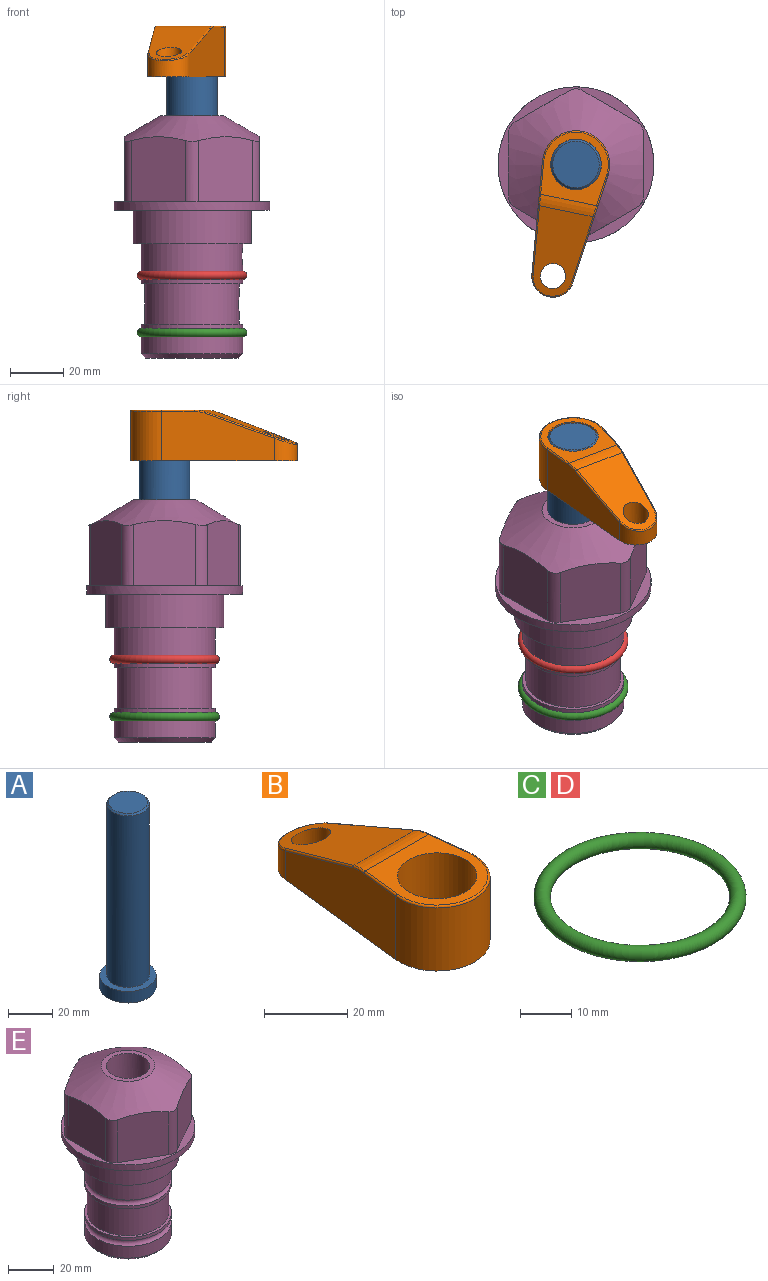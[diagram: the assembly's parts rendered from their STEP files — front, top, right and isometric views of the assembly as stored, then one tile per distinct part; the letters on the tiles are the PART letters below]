
ASSEMBLY  parts=5 mates=3
PART A: 6 faces, bbox 25.4x25.4x101.6 mm
  f0: plane 17.46x17.46mm, normal (0,0,1), area 239.5mm2, adj f5
  f1: plane 25.4x25.4mm, normal (0,0,-1), area 506.7mm2, adj f2
  f2: cylinder r=12.7mm len=25.4mm, axis (0,0,1), area 506.7mm2, adj f1,f3
  f3: plane 25.4x25.4mm, normal (0,0,1), area 221.7mm2, adj f2,f4
  f4: cylinder r=9.53mm len=94.46mm, axis (0,0,1), area 5653mm2, adj f3,f5
  f5: cone r=8.73mm half-angle=45deg, axis (0,0,-1), area 64.4mm2, adj f0,f4
PART B: 44 faces, bbox 27.5x64.5x19.1 mm
  f0: plane 2.3x0.95mm, normal (0,0,-1), area 1mm2, adj f25,f30,f34
  f1: plane 63.5x25.4mm, normal (0,0,-1), area 561.7mm2, adj f2,f3,f4,f5,f6,f7,f19,f20
  f2: cylinder r=12.7mm len=25.4mm, axis (0,0,-1), area 792.2mm2, adj f1,f3,f5,f13
  f3: plane 42.33x18.54mm, normal (0.99,0.11,0), area 647mm2, adj f1,f2,f4,f11,f12,f14
  f4: cylinder r=7.94mm len=15.78mm, axis (0,0,-1), area 158.6mm2, adj f1,f3,f5,f16
  f5: plane 42.33x18.54mm, normal (-0.99,0.11,0), area 647mm2, adj f1,f2,f4,f15,f17,f18
  f6: cylinder r=9.53mm len=19.05mm, axis (0,0,-1), area 1140.1mm2, adj f1,f8
  f7: cylinder r=4.76mm len=10.98mm, axis (0,0,-1), area 276.1mm2, adj f1,f9
  f8: plane 25.83x24.38mm, normal (0,0,1), area 262.2mm2, adj f6,f10,f11,f13,f15
  f9: plane 32.49x20.55mm, normal (0,0.34,0.94), area 489.9mm2, adj f7,f10,f14,f16,f18
  f10: cylinder r=12.7mm len=21.49mm, axis (-1,0,0), area 93.2mm2, adj f8,f9,f12,f17
  f11: cylinder r=0.51mm len=12.34mm, axis (0.11,-0.99,0), area 9.9mm2, adj f3,f8,f12,f13
  f12: bspline ~7.62x1.64mm, area 3.5mm2, adj f3,f10,f11,f14
  f13: torus R=12.19mm, axis (0,0,1), area 33.6mm2, adj f2,f8,f11,f15
  f14: cylinder r=0.51mm len=26.01mm, axis (0.1,-0.93,0.34), area 21.6mm2, adj f3,f9,f12,f16
  f15: cylinder r=0.51mm len=12.34mm, axis (0.11,0.99,0), area 9.9mm2, adj f5,f8,f13,f17
  f16: bspline ~15.78x7.05mm, area 15.7mm2, adj f4,f9,f14,f18
  f17: bspline ~7.62x1.64mm, area 3.5mm2, adj f5,f10,f15,f18
  f18: cylinder r=0.51mm len=26.01mm, axis (0.1,0.93,-0.34), area 21.6mm2, adj f5,f9,f16,f17
  f19: plane 21.6x14.29mm, normal (-0.99,-0.11,0), area 242.6mm2, adj f1,f26,f28,f34,f36,f38
  f20: plane 21.6x14.29mm, normal (0.99,-0.11,0), area 242.6mm2, adj f1,f27,f29,f37,f39,f41
  f21: cylinder r=12.7mm len=14.29mm, axis (0,0,-1), area 173.2mm2, adj f1,f26,f27,f30,f31,f33
  f22: cylinder r=7.94mm len=7.63mm, axis (0,0,-1), area 53.8mm2, adj f1,f28,f29,f42
  f23: plane 2.3x0.95mm, normal (0,0,-1), area 1mm2, adj f25,f33,f37
  f24: plane 17.94x12.32mm, normal (0,-0.34,-0.94), area 191.2mm2, adj f25,f38,f41,f42
  f25: cylinder r=9.53mm len=12.93mm, axis (-1,0,0), area 37.5mm2, adj f0,f23,f24,f31,f36,f39
  f26: cylinder r=1.59mm len=14.29mm, axis (0,0,-1), area 49mm2, adj f1,f19,f21,f32
  f27: cylinder r=1.59mm len=14.29mm, axis (0,0,-1), area 49mm2, adj f1,f20,f21,f35
  f28: cylinder r=1.59mm len=7.28mm, axis (0,0,-1), area 22.1mm2, adj f1,f19,f22,f40
  f29: cylinder r=1.59mm len=7.28mm, axis (0,0,-1), area 22.1mm2, adj f1,f20,f22,f43
  f30: torus R=14.29mm, axis (0,0,1), area 5.8mm2, adj f0,f21,f31,f32
  f31: bspline ~11.06x2.73mm, area 20.8mm2, adj f21,f25,f30,f33
  f32: sphere r=1.59mm, area 5.4mm2, adj f26,f30,f34
  f33: torus R=14.29mm, axis (0,0,1), area 5.8mm2, adj f21,f23,f31,f35
  f34: cylinder r=1.59mm len=1.68mm, axis (-0.11,0.99,0), area 2.4mm2, adj f0,f19,f32,f36
  f35: sphere r=1.59mm, area 5.4mm2, adj f27,f33,f37
  f36: bspline ~5.82x2.33mm, area 7.7mm2, adj f19,f25,f34,f38
  f37: cylinder r=1.59mm len=1.68mm, axis (0.11,0.99,0), area 2.4mm2, adj f20,f23,f35,f39
  f38: cylinder r=1.59mm len=18.33mm, axis (0.1,-0.93,0.34), area 46.7mm2, adj f19,f24,f36,f40
  f39: bspline ~5.82x2.33mm, area 7.7mm2, adj f20,f25,f37,f41
  f40: sphere r=1.59mm, area 3.6mm2, adj f28,f38,f42
  f41: cylinder r=1.59mm len=18.33mm, axis (0.1,0.93,-0.34), area 46.7mm2, adj f20,f24,f39,f43
  f42: bspline ~8.31x1.84mm, area 15.3mm2, adj f22,f24,f40,f43
  f43: sphere r=1.59mm, area 3.6mm2, adj f29,f41,f42
PART C: 1 faces, bbox 44.7x44.7x3.2 mm
  f0: torus R=19.05mm, axis (0,0,1), area 1193.9mm2
PART D: same geometry as C
PART E: 36 faces, bbox 58.7x58.7x91.2 mm
  f0: cylinder r=17.78mm len=35.56mm, axis (0,0,1), area 1670.8mm2, adj f23,f24,f31
  f1: cylinder r=19.05mm len=38.1mm, axis (0,0,1), area 1191.9mm2, adj f26,f27,f30
  f2: plane 58.66x58.66mm, normal (0,0,-1), area 1150.6mm2, adj f3,f28
  f3: cylinder r=29.33mm len=58.66mm, axis (0,0,-1), area 585.1mm2, adj f2,f4
  f4: plane 58.66x58.66mm, normal (0,0,1), area 475.9mm2, adj f3,f5,f6,f7,f8,f9,f10,f11
  f5: plane 24.5x20.32mm, normal (-0.5,0.87,0), area 562.8mm2, adj f4,f15,f16,f17
  f6: plane 24.5x20.32mm, normal (0.5,0.87,0), area 562.8mm2, adj f4,f14,f15,f17
  f7: plane 24.5x23.48mm, normal (1,0,0), area 562.8mm2, adj f4,f13,f14,f17
  f8: plane 24.5x20.32mm, normal (0.5,-0.87,0), area 562.8mm2, adj f4,f12,f13,f17
  f9: plane 24.5x20.32mm, normal (-0.5,-0.87,0), area 562.8mm2, adj f4,f11,f12,f17
  f10: plane 24.5x23.48mm, normal (-1,0,0), area 562.8mm2, adj f4,f11,f16,f17
  f11: cylinder r=5.08mm len=23.01mm, axis (0,0,-1), area 121.2mm2, adj f4,f9,f10,f17
  f12: cylinder r=5.08mm len=23.01mm, axis (0,0,-1), area 121.2mm2, adj f4,f8,f9,f17
  f13: cylinder r=5.08mm len=23.01mm, axis (0,0,-1), area 121.2mm2, adj f4,f7,f8,f17
  f14: cylinder r=5.08mm len=23.01mm, axis (0,0,-1), area 121.2mm2, adj f4,f6,f7,f17
  f15: cylinder r=5.08mm len=23.01mm, axis (0,0,-1), area 121.2mm2, adj f4,f5,f6,f17
  f16: cylinder r=5.08mm len=23.01mm, axis (0,0,-1), area 121.2mm2, adj f4,f5,f10,f17
  f17: cone r=11.73mm half-angle=60deg, axis (0,0,-1), area 2071.8mm2, adj f5,f6,f7,f8,f9,f10,f11,f12
  f18: plane 23.46x23.46mm, normal (0,0,1), area 147.4mm2, adj f17,f35
  f19: plane 34.93x34.93mm, normal (0,0,-1), area 958mm2, adj f29
  f20: cylinder r=19.05mm len=38.1mm, axis (0,0,1), area 760.1mm2, adj f21,f29
  f21: torus R=19.05mm, axis (0,0,1), area 565.3mm2, adj f20,f22
  f22: cylinder r=19.05mm len=38.1mm, axis (0,0,1), area 190mm2, adj f21,f23
  f23: plane 38.1x38.1mm, normal (0,0,1), area 146.9mm2, adj f0,f22
  f24: plane 38.1x38.1mm, normal (0,0,-1), area 146.9mm2, adj f0,f25
  f25: cylinder r=19.05mm len=38.1mm, axis (0,0,1), area 190mm2, adj f24,f26
  f26: torus R=19.05mm, axis (0,0,1), area 565.3mm2, adj f1,f25
  f27: plane 44.45x44.45mm, normal (0,0,-1), area 411.7mm2, adj f1,f28
  f28: cylinder r=22.23mm len=44.45mm, axis (0,0,1), area 1773.5mm2, adj f2,f27
  f29: cone r=19.05mm half-angle=45deg, axis (0,0,1), area 257.5mm2, adj f19,f20
  f30: cylinder r=3.17mm len=6.75mm, axis (-1,0,0), area 128mm2, adj f1,f33
  f31: cylinder r=3.17mm len=6.35mm, axis (-1,0,0), area 102.5mm2, adj f0,f33
  f32: plane 25.4x25.4mm, normal (0,0,1), area 506.7mm2, adj f33
  f33: cylinder r=12.7mm len=66.42mm, axis (0,0,-1), area 5236.2mm2, adj f30,f31,f32,f34
  f34: cone r=9.53mm half-angle=30deg, axis (0,0,-1), area 443.4mm2, adj f33,f35
  f35: cylinder r=9.53mm len=19.05mm, axis (0,0,-1), area 849mm2, adj f18,f34
PLACE A rot(axis=(0,0,-1),101.7deg) t=(0,0,-4.35)mm
PLACE B rot(axis=(0,0,1),168.3deg) t=(0,0,50.26)mm
PLACE C t=(0,0,-21.59)mm
PLACE D at identity
PLACE E at identity fixed
MATE fastened C.f0 <-> E.f0  axis (0,0,1) through (0,0,-46.1)mm
MATE cylindrical A.f2 <-> E.f0  axis (0,0,1) through (0,0,21.29)mm
MATE fastened B.f2 <-> A.f2  axis (0,0,1) through (0,0,69.31)mm
